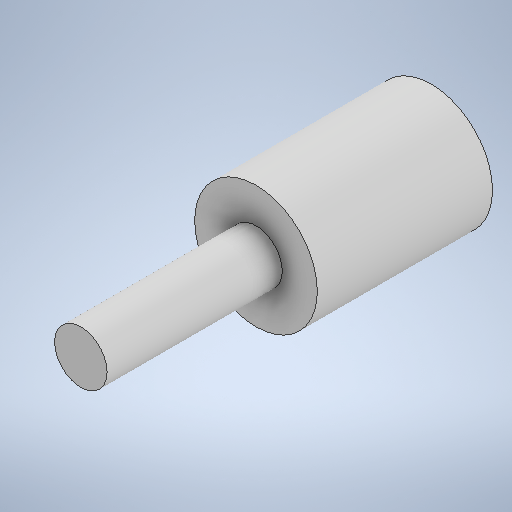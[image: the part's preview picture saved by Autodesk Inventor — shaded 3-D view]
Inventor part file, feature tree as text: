
AUTODESK INVENTOR PART (.ipt)
format: ipt  version: 2025.3 (Build 293356000, 356)  size: 230,400 bytes
history: native  units: mm
features: extrude x3, sketch x3, other x1
ambient origin geometry x8: Origin, YZ Plane, XZ Plane, XY Plane, X Axis, Y Axis, Z Axis, Center Point
bodies: Body1 (feature_tree)
feature tree (7):
  other  "Sólido1"
  extrude  "Extrusión1"  Depth=20.0mm TaperAngle=0.0deg
  extrude  "Extrusión2"  Depth=2.5mm TaperAngle=0.0deg
  extrude  "Extrusión3"  Depth=20.0mm TaperAngle=0.0deg
  sketch  "Boceto1"  dims[d0=14.0mm d1=20.0mm d2=0.0mm]
  sketch  "Boceto2"  dims[d3=2.0mm d4=2.5mm d5=0.0mm]
  sketch  "Boceto3"  dims[d6=6.0mm d7=20.0mm d8=0.0mm]
